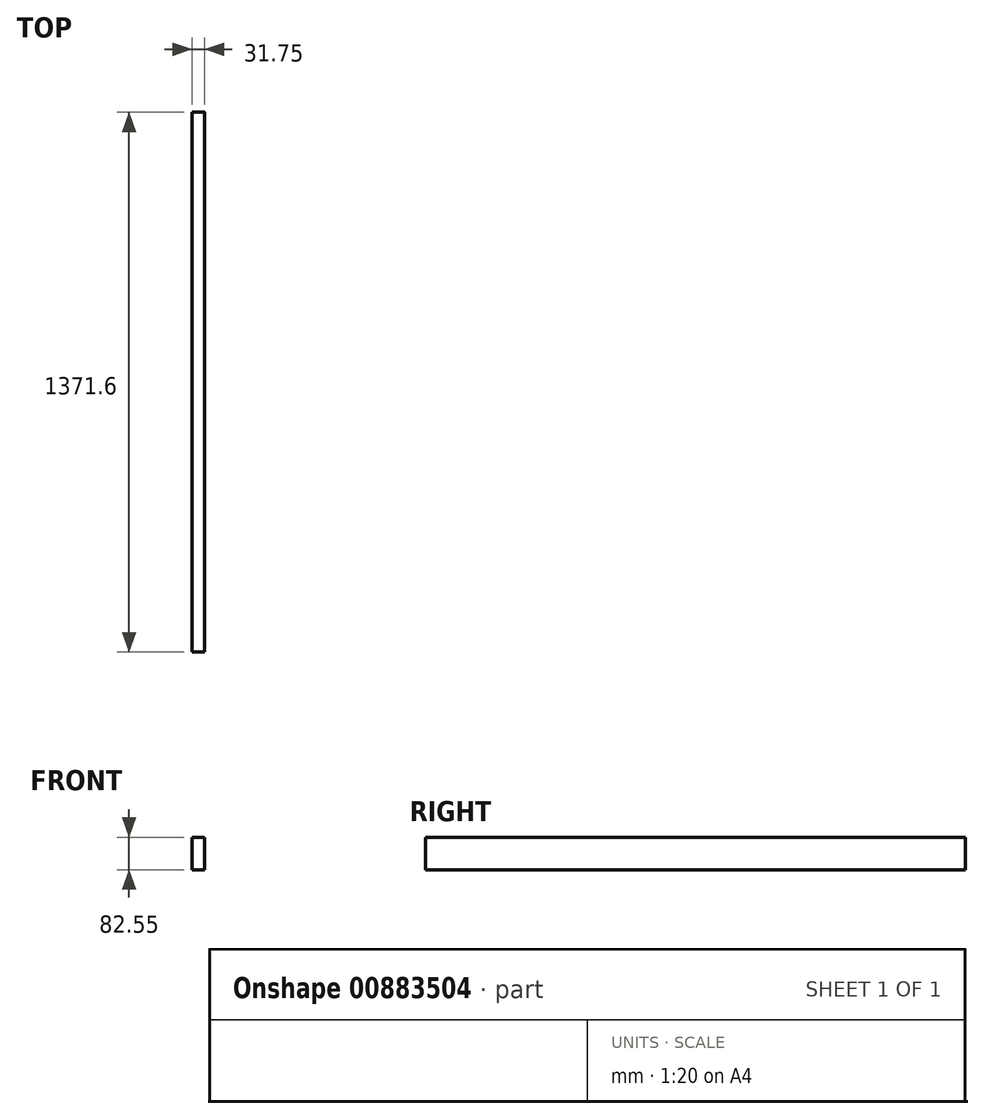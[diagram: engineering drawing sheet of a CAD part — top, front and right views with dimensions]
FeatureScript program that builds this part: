
annotation { "Feature Type Name" : "Feature", "Feature Type Description" : "" }
export const myFeature = defineFeature(function(context is Context, id is Id, definition is map)
    precondition{}
    {
        {
            var Q0;
            Q0=qCreatedBy(makeId("Front.planeOp"),FACE);
            var sketch = newSketch(context, id + "F0", { "sketchPlane" : qUnion([Q0])});
            skLineSegment(sketch, "E0.bottom", {"start": v(0, 0) * mm, "end": v(31.75, 0) * mm});
            skLineSegment(sketch, "E0.top", {"start": v(0, 82.55) * mm, "end": v(31.75, 82.55) * mm});
            skLineSegment(sketch, "E0.left", {"start": v(0, 0) * mm, "end": v(0, 82.55) * mm});
            skLineSegment(sketch, "E0.right", {"start": v(31.75, 0) * mm, "end": v(31.75, 82.55) * mm});
            skSolve(sketch);
        }
        {
            var Q0;
            Q0 = qSketchRegion(id + "F0", true);
            extrude(context, id + "F1", {"entities" : qUnion([Q0]), "oppositeDirection" : true, "depth" : 1371.6 * mm, "offsetDistance" : 25.4 * mm});
        }
        {
            var Q0;
            Q0=makeQuery(id+"F1.opExtrude","SWEPT_EDGE",EDGE,{"disambiguationData":[OSD([sQuery(id+"F0.wireOp",EDGE,"E0.top"),sQuery(id+"F0.wireOp",EDGE,"E0.right")])]});
            fillet(context, id + "F2", {"entities" : qUnion([Q0]), "radius" : 4.76 * mm, "tangentPropagation" : true, "allowEdgeOverflow" : false});
        }
    });
